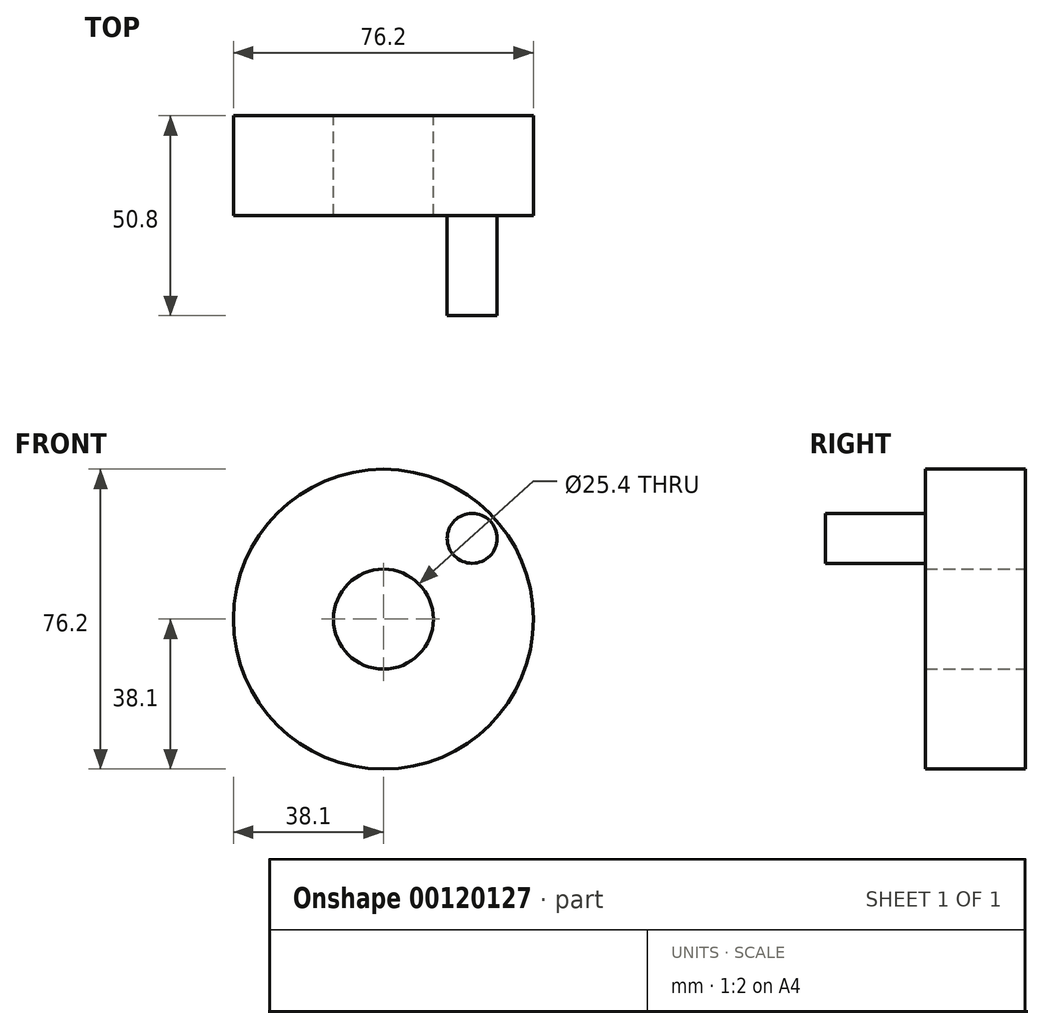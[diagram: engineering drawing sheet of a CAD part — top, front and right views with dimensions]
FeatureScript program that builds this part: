
annotation { "Feature Type Name" : "Feature", "Feature Type Description" : "" }
export const myFeature = defineFeature(function(context is Context, id is Id, definition is map)
    precondition{}
    {
        {
            var Q0;
            Q0=qCreatedBy(makeId("Front.planeOp"),FACE);
            var sketch = newSketch(context, id + "F0", { "sketchPlane" : qUnion([Q0])});
            skCircle(sketch, "E0", {"center": v(0, 0) * mm, "radius": 12.7 * mm});
            skLineSegment(sketch, "E1", {"start": v(0, 0) * mm, "end": v(0, 38.1) * mm, "construction": true});
            skCircle(sketch, "E2", {"center": v(0, 0) * mm, "radius": 38.1 * mm});
            skSolve(sketch);
        }
        {
            var Q0;
            Q0 = qSketchRegion(id + "F0", true);
            extrude(context, id + "F1", {"entities" : qUnion([Q0]), "endBound" : BoundingType.SYMMETRIC, "depth" : 25.4 * mm});
        }
        {
            var Q0;
            Q0=makeQuery(id+"F1.opExtrude","CAP_FACE",FACE,{"disambiguationData":[OSD([sQuery(id+"F0.wireOp",EDGE,"E0"),sQuery(id+"F0.wireOp",EDGE,"E2")])],"isStart":false});
            var sketch = newSketch(context, id + "F2", { "sketchPlane" : qUnion([Q0])});
            skCircle(sketch, "E3", {"center": v(22.56, 20.54) * mm, "radius": 6.35 * mm});
            skSolve(sketch);
        }
        {
            var Q0;
            Q0=makeQuery(id+"F2.imprint","IMPRINT",FACE,{"disambiguationData":[TD([[makeQuery(id+"F2.imprint","IMPRINT",EDGE,{"derivedFrom":sQuery(id+"F2.wireOp",EDGE,"RAIiBvS5-2MtS-FTpL-01tM-50iirGGtwXNx")}),1.0]])]});
            var Q1;
            Q1=makeQuery(id+"F2.imprint","IMPRINT",FACE,{"disambiguationData":[TD([[makeQuery(id+"F2.imprint","IMPRINT",EDGE,{"derivedFrom":sQuery(id+"F2.wireOp",EDGE,"E3")}),1.0]])]});
            extrude(context, id + "F3", {"entities" : qUnion([Q0, Q1]), "operationType" : NewBodyOperationType.ADD, "depth" : 25.4 * mm});
        }
    });
